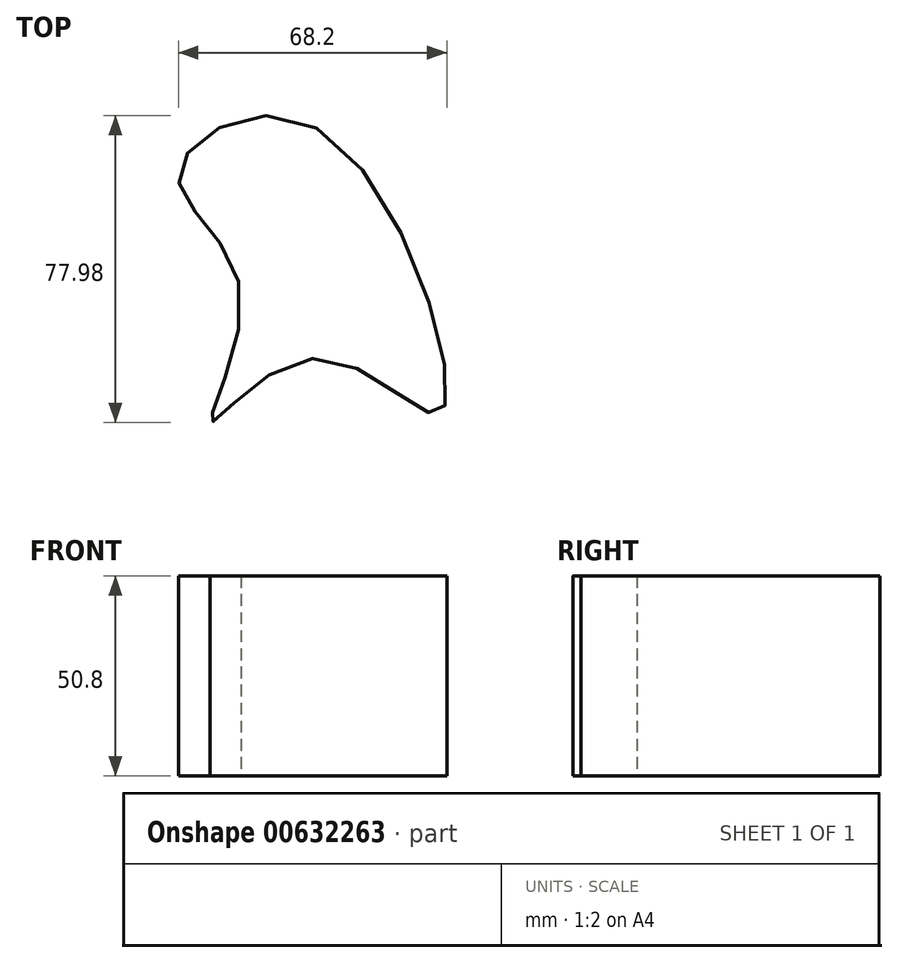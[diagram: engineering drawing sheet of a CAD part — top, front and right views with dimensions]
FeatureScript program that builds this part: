
annotation { "Feature Type Name" : "Feature", "Feature Type Description" : "" }
export const myFeature = defineFeature(function(context is Context, id is Id, definition is map)
    precondition{}
    {
        {
            var Q0;
            Q0=qCreatedBy(makeId("Top.planeOp"),FACE);
            var sketch = newSketch(context, id + "F0", { "sketchPlane" : qUnion([Q0])});
            skFitSpline(sketch, "E0", {"points": [v(0, 40.57) * mm, v(-35.01, 29.09) * mm, v(-19.45, 0) * mm, v(-26.86, -34.27) * mm, v(0, -17.97) * mm, v(31.68, -31.68) * mm, v(0, 40.57) * mm]});
            skSolve(sketch);
        }
        {
            var Q0;
            Q0=makeQuery(id+"F0.imprint","IMPRINT",FACE,{"disambiguationData":[TD([[makeQuery(id+"F0.imprint","IMPRINT",EDGE,{"derivedFrom":sQuery(id+"F0.wireOp",EDGE,"E0")}),1.0]])]});
            extrude(context, id + "F1", {"entities" : qUnion([Q0]), "depth" : 50.8 * mm, "offsetDistance" : 25.4 * mm});
        }
    });
